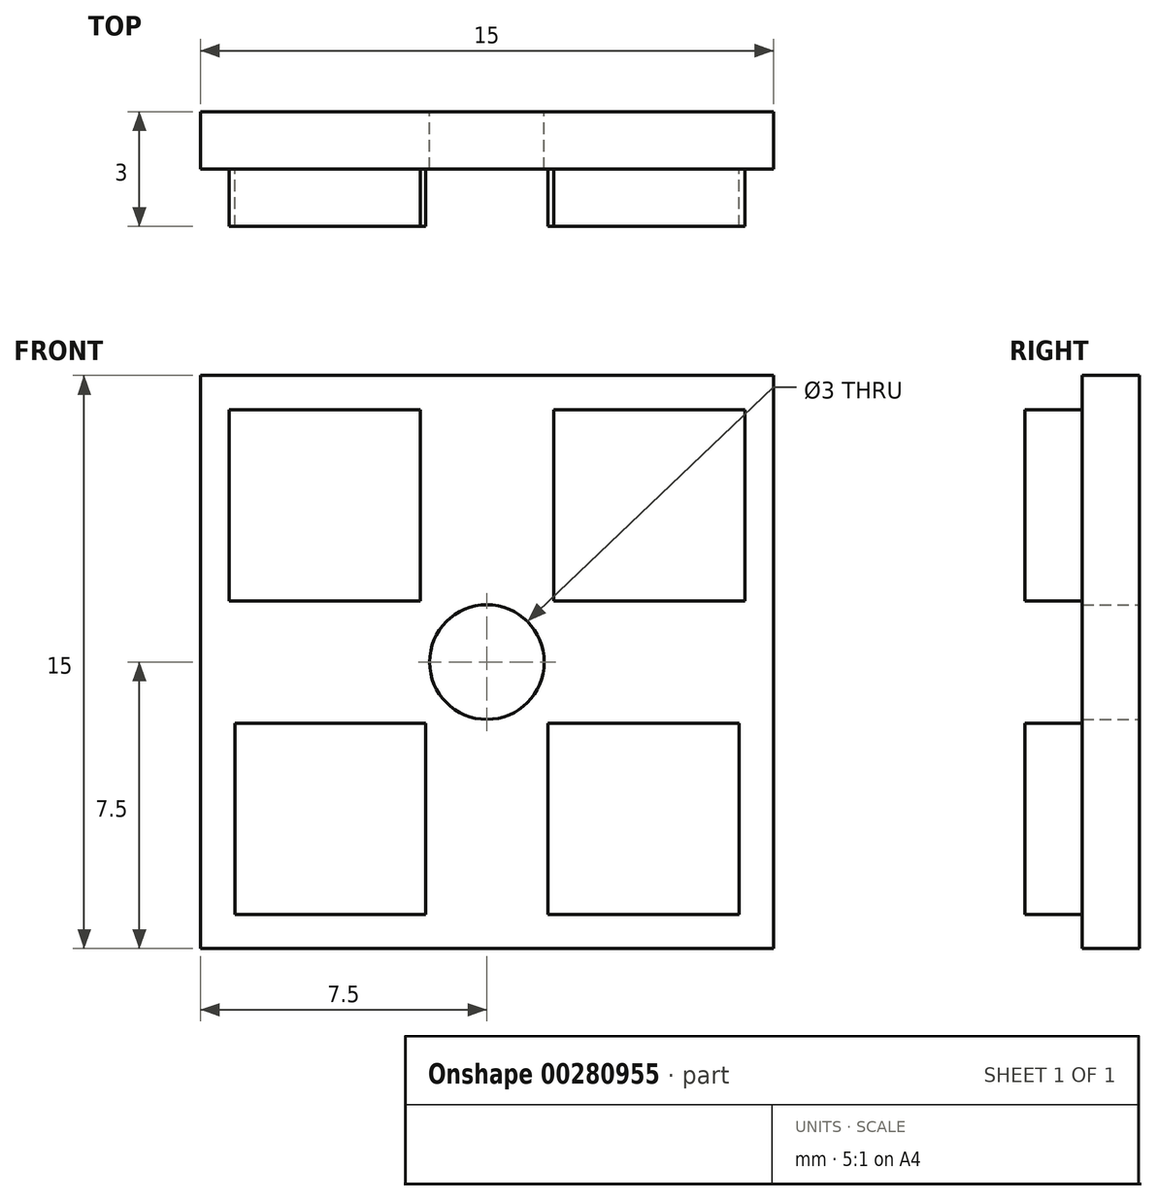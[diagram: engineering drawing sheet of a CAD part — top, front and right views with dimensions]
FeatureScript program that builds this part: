
annotation { "Feature Type Name" : "Feature", "Feature Type Description" : "" }
export const myFeature = defineFeature(function(context is Context, id is Id, definition is map)
    precondition{}
    {
        {
            var Q0;
            Q0=qCreatedBy(makeId("Front.planeOp"),FACE);
            var sketch = newSketch(context, id + "F0", { "sketchPlane" : qUnion([Q0])});
            skLineSegment(sketch, "E0.bottom", {"start": v(-7.5, 7.5) * mm, "end": v(7.5, 7.5) * mm});
            skLineSegment(sketch, "E0.top", {"start": v(-7.5, -7.5) * mm, "end": v(7.5, -7.5) * mm});
            skLineSegment(sketch, "E0.left", {"start": v(-7.5, 7.5) * mm, "end": v(-7.5, -7.5) * mm});
            skLineSegment(sketch, "E0.right", {"start": v(7.5, 7.5) * mm, "end": v(7.5, -7.5) * mm});
            skCircle(sketch, "E1", {"center": v(0, 0) * mm, "radius": 1.5 * mm});
            skSolve(sketch);
        }
        {
            var Q0;
            Q0=makeQuery(id+"F0.imprint","IMPRINT",FACE,{"disambiguationData":[TD([[makeQuery(id+"F0.imprint","IMPRINT",EDGE,{"derivedFrom":sQuery(id+"F0.wireOp",EDGE,"E0.bottom")}),-1.0]])]});
            extrude(context, id + "F1", {"entities" : qUnion([Q0]), "depth" : 1.5 * mm});
        }
        {
            var Q0;
            Q0=makeQuery(id+"F1.opExtrude","CAP_FACE",FACE,{"disambiguationData":[OSD([sQuery(id+"F0.wireOp",EDGE,"E0.bottom"),sQuery(id+"F0.wireOp",EDGE,"E0.top"),sQuery(id+"F0.wireOp",EDGE,"E0.left"),sQuery(id+"F0.wireOp",EDGE,"E0.right"),sQuery(id+"F0.wireOp",EDGE,"E1")])],"isStart":false});
            var sketch = newSketch(context, id + "F2", { "sketchPlane" : qUnion([Q0])});
            skLineSegment(sketch, "E2.bottom", {"start": v(-6.75, 6.6) * mm, "end": v(-1.75, 6.6) * mm});
            skLineSegment(sketch, "E2.top", {"start": v(-6.75, 1.6) * mm, "end": v(-1.75, 1.6) * mm});
            skLineSegment(sketch, "E2.left", {"start": v(-6.75, 6.6) * mm, "end": v(-6.75, 1.6) * mm});
            skLineSegment(sketch, "E2.right", {"start": v(-1.75, 6.6) * mm, "end": v(-1.75, 1.6) * mm});
            skLineSegment(sketch, "E3.bottom", {"start": v(1.75, 6.6) * mm, "end": v(6.75, 6.6) * mm});
            skLineSegment(sketch, "E3.top", {"start": v(1.75, 1.6) * mm, "end": v(6.75, 1.6) * mm});
            skLineSegment(sketch, "E3.left", {"start": v(1.75, 6.6) * mm, "end": v(1.75, 1.6) * mm});
            skLineSegment(sketch, "E3.right", {"start": v(6.75, 6.6) * mm, "end": v(6.75, 1.6) * mm});
            skLineSegment(sketch, "E4.bottom", {"start": v(-6.6, -1.6) * mm, "end": v(-1.6, -1.6) * mm});
            skLineSegment(sketch, "E4.top", {"start": v(-6.6, -6.6) * mm, "end": v(-1.6, -6.6) * mm});
            skLineSegment(sketch, "E4.left", {"start": v(-6.6, -1.6) * mm, "end": v(-6.6, -6.6) * mm});
            skLineSegment(sketch, "E4.right", {"start": v(-1.6, -1.6) * mm, "end": v(-1.6, -6.6) * mm});
            skLineSegment(sketch, "E5.bottom", {"start": v(1.6, -1.6) * mm, "end": v(6.6, -1.6) * mm});
            skLineSegment(sketch, "E5.top", {"start": v(1.6, -6.6) * mm, "end": v(6.6, -6.6) * mm});
            skLineSegment(sketch, "E5.left", {"start": v(1.6, -1.6) * mm, "end": v(1.6, -6.6) * mm});
            skLineSegment(sketch, "E5.right", {"start": v(6.6, -1.6) * mm, "end": v(6.6, -6.6) * mm});
            skSolve(sketch);
        }
        {
            var Q0;
            Q0 = qSketchRegion(id + "F2", true);
            extrude(context, id + "F3", {"entities" : qUnion([Q0]), "operationType" : NewBodyOperationType.ADD, "depth" : 1.5 * mm});
        }
    });
